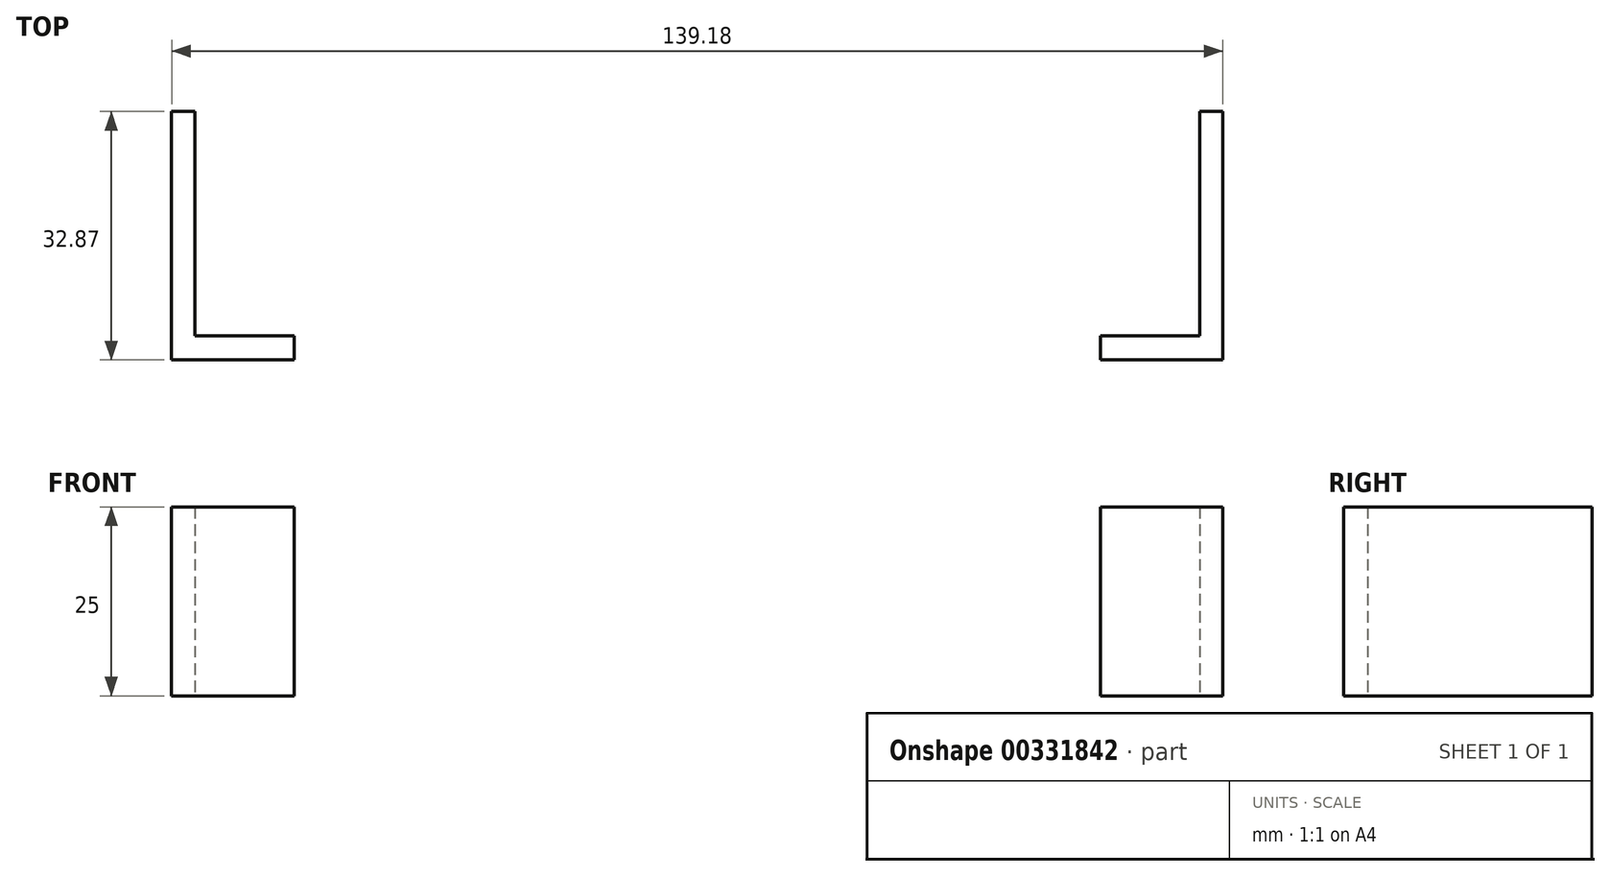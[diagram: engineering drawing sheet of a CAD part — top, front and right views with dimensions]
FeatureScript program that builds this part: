
annotation { "Feature Type Name" : "Feature", "Feature Type Description" : "" }
export const myFeature = defineFeature(function(context is Context, id is Id, definition is map)
    precondition{}
    {
        {
            var Q0;
            Q0=qCreatedBy(makeId("Top.planeOp"),FACE);
            var sketch = newSketch(context, id + "F0", { "sketchPlane" : qUnion([Q0])});
            skLineSegment(sketch, "E0", {"start": v(-69.6, 0) * mm, "end": v(-69.6, 32.87) * mm});
            skLineSegment(sketch, "E1", {"start": v(-69.6, 32.87) * mm, "end": v(-66.5, 32.87) * mm});
            skLineSegment(sketch, "E2", {"start": v(-66.5, 32.87) * mm, "end": v(-66.5, 3.18) * mm});
            skLineSegment(sketch, "E3", {"start": v(-66.5, 3.18) * mm, "end": v(-53.4, 3.18) * mm});
            skLineSegment(sketch, "E4", {"start": v(-53.4, 3.18) * mm, "end": v(-53.4, 0) * mm});
            skLineSegment(sketch, "E5", {"start": v(-53.4, 0) * mm, "end": v(-69.6, 0) * mm});
            skLineSegment(sketch, "E6.MirrorCS", {"start": v(66.5, 32.87) * mm, "end": v(66.5, 3.18) * mm});
            skLineSegment(sketch, "E7.MirrorCS", {"start": v(69.6, 0) * mm, "end": v(69.6, 32.87) * mm});
            skLineSegment(sketch, "E8.MirrorCS", {"start": v(53.4, 0) * mm, "end": v(69.6, 0) * mm});
            skLineSegment(sketch, "E9.MirrorCS", {"start": v(66.5, 3.18) * mm, "end": v(53.4, 3.18) * mm});
            skLineSegment(sketch, "E10.MirrorCS", {"start": v(53.4, 3.18) * mm, "end": v(53.4, 0) * mm});
            skLineSegment(sketch, "E11", {"start": v(66.5, 32.87) * mm, "end": v(69.6, 32.87) * mm});
            skLineSegment(sketch, "E12", {"start": v(-66.5, 29.6) * mm, "end": v(-66.5, 26.12) * mm});
            skLineSegment(sketch, "E13", {"start": v(66.5, 26.12) * mm, "end": v(66.5, 29.4) * mm});
            skLineSegment(sketch, "E14", {"start": v(-65.16, 29.6) * mm, "end": v(-50.5, 29.6) * mm});
            skLineSegment(sketch, "E15", {"start": v(-50.5, 29.6) * mm, "end": v(-50.5, 25.35) * mm});
            skLineSegment(sketch, "E16", {"start": v(-50.5, 25.35) * mm, "end": v(-66.5, 26.12) * mm});
            skSolve(sketch);
        }
        {
            var Q0;
            Q0=makeQuery(id+"F0.imprint","IMPRINT",FACE,{"disambiguationData":[TD([[makeQuery(id+"F0.imprint","IMPRINT",EDGE,{"derivedFrom":sQuery(id+"F0.wireOp",EDGE,"E0")}),-1.0]])]});
            extrude(context, id + "F1", {"entities" : qUnion([Q0]), "depth" : 25 * mm});
        }
        {
            var Q0;
            Q0=makeQuery(id+"F0.imprint","IMPRINT",FACE,{"disambiguationData":[TD([[makeQuery(id+"F0.imprint","IMPRINT",EDGE,{"derivedFrom":sQuery(id+"F0.wireOp",EDGE,"E7.MirrorCS")}),1.0]])]});
            extrude(context, id + "F2", {"entities" : qUnion([Q0]), "operationType" : NewBodyOperationType.ADD, "depth" : 25 * mm});
        }
    });
